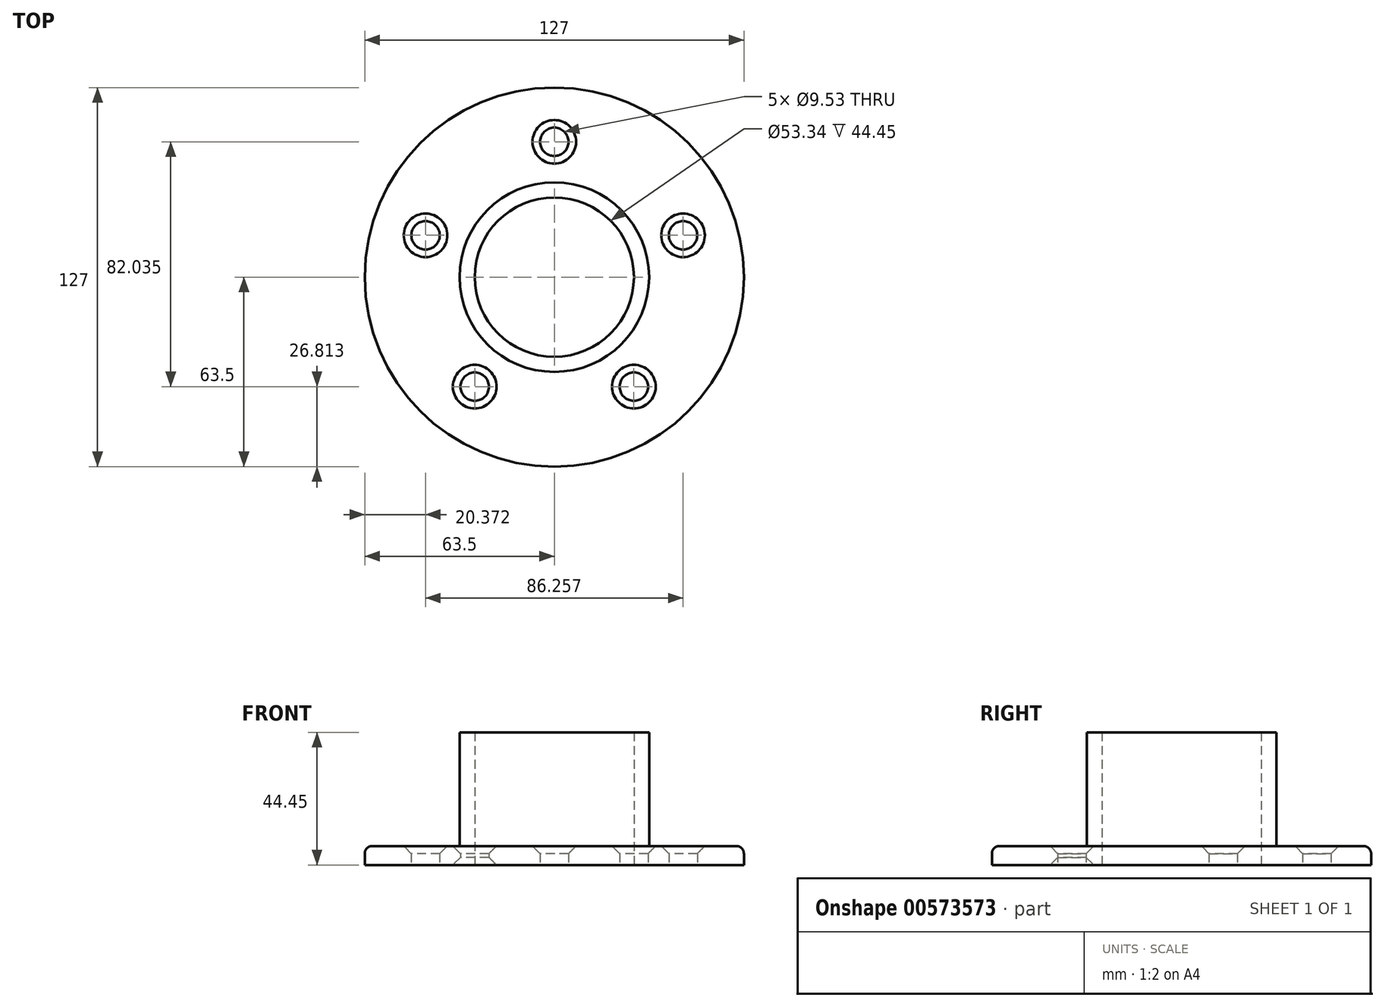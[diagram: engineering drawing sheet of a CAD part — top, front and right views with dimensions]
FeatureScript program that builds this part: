
annotation { "Feature Type Name" : "Feature", "Feature Type Description" : "" }
export const myFeature = defineFeature(function(context is Context, id is Id, definition is map)
    precondition{}
    {
        {
            var Q0;
            Q0=qCreatedBy(makeId("Top.planeOp"),FACE);
            var sketch = newSketch(context, id + "F0", { "sketchPlane" : qUnion([Q0])});
            skCircle(sketch, "E0", {"center": v(0, 0) * mm, "radius": 63.5 * mm});
            skCircle(sketch, "E1", {"center": v(0, 0) * mm, "radius": 26.67 * mm});
            skLineSegment(sketch, "E2", {"start": v(0, 63.5) * mm, "end": v(0, -63.5) * mm, "construction": true});
            skLineSegment(sketch, "E3", {"start": v(63.5, 0) * mm, "end": v(-63.5, 0) * mm, "construction": true});
            skCircle(sketch, "E4", {"center": v(0, 45.35) * mm, "radius": 4.76 * mm});
            skCircle(sketch, "E5.1.0", {"center": v(-43.13, 14.01) * mm, "radius": 4.76 * mm});
            skCircle(sketch, "E5.2.0", {"center": v(-26.65, -36.69) * mm, "radius": 4.76 * mm});
            skCircle(sketch, "E5.3.0", {"center": v(26.65, -36.69) * mm, "radius": 4.76 * mm});
            skCircle(sketch, "E5.4.0", {"center": v(43.13, 14.01) * mm, "radius": 4.76 * mm});
            skSolve(sketch);
        }
        {
            var Q0;
            Q0 = qSketchRegion(id + "F0", true);
            extrude(context, id + "F1", {"entities" : qUnion([Q0]), "depth" : 6.35 * mm, "offsetDistance" : 25.4 * mm});
        }
        {
            var Q0;
            Q0=makeQuery(id+"F1.opExtrude","CAP_FACE",FACE,{"disambiguationData":[OSD([sQuery(id+"F0.wireOp",EDGE,"E0")])],"isStart":false});
            var sketch = newSketch(context, id + "F2", { "sketchPlane" : qUnion([Q0])});
            skCircle(sketch, "E6", {"center": v(0, 0) * mm, "radius": 31.75 * mm});
            skCircle(sketch, "E7", {"center": v(0, 0) * mm, "radius": 26.67 * mm});
            skSolve(sketch);
        }
        {
            var Q0;
            Q0 = qSketchRegion(id + "F2", true);
            extrude(context, id + "F3", {"entities" : qUnion([Q0]), "operationType" : NewBodyOperationType.ADD, "depth" : 38.1 * mm, "offsetDistance" : 25.4 * mm});
        }
        {
            var Q0;
            Q0=makeQuery(id+"F3.opExtrude","CAP_EDGE",EDGE,{"disambiguationData":[OSD([sQuery(id+"F2.wireOp",EDGE,"E6")])],"isStart":true});
            var Q1;
            Q1=makeQuery(id+"F1.opExtrude","CAP_EDGE",EDGE,{"disambiguationData":[OSD([sQuery(id+"F0.wireOp",EDGE,"E0")])],"isStart":false});
            fillet(context, id + "F4", {"entities" : qUnion([Q0, Q1]), "radius" : 2.54 * mm, "tangentPropagation" : true, "allowEdgeOverflow" : false});
        }
        {
            var Q0;
            Q0=makeQuery(id+"F1.opExtrude","CAP_EDGE",EDGE,{"disambiguationData":[OSD([sQuery(id+"F0.wireOp",EDGE,"E5.1.0")])],"isStart":false});
            var Q1;
            Q1=makeQuery(id+"F1.opExtrude","SWEPT_FACE",FACE,{"disambiguationData":[OSD([sQuery(id+"F0.wireOp",EDGE,"E5.2.0")])]});
            var Q2;
            Q2=makeQuery(id+"F1.opExtrude","CAP_EDGE",EDGE,{"disambiguationData":[OSD([sQuery(id+"F0.wireOp",EDGE,"E5.3.0")])],"isStart":false});
            var Q3;
            Q3=makeQuery(id+"F1.opExtrude","CAP_EDGE",EDGE,{"disambiguationData":[OSD([sQuery(id+"F0.wireOp",EDGE,"E5.4.0")])],"isStart":false});
            var Q4;
            Q4=makeQuery(id+"F1.opExtrude","CAP_EDGE",EDGE,{"disambiguationData":[OSD([sQuery(id+"F0.wireOp",EDGE,"E4")])],"isStart":false});
            chamfer(context, id + "F5", {"entities" : qUnion([Q0, Q1, Q2, Q3, Q4]), "width" : 2.54 * mm, "tangentPropagation" : true});
        }
    });
